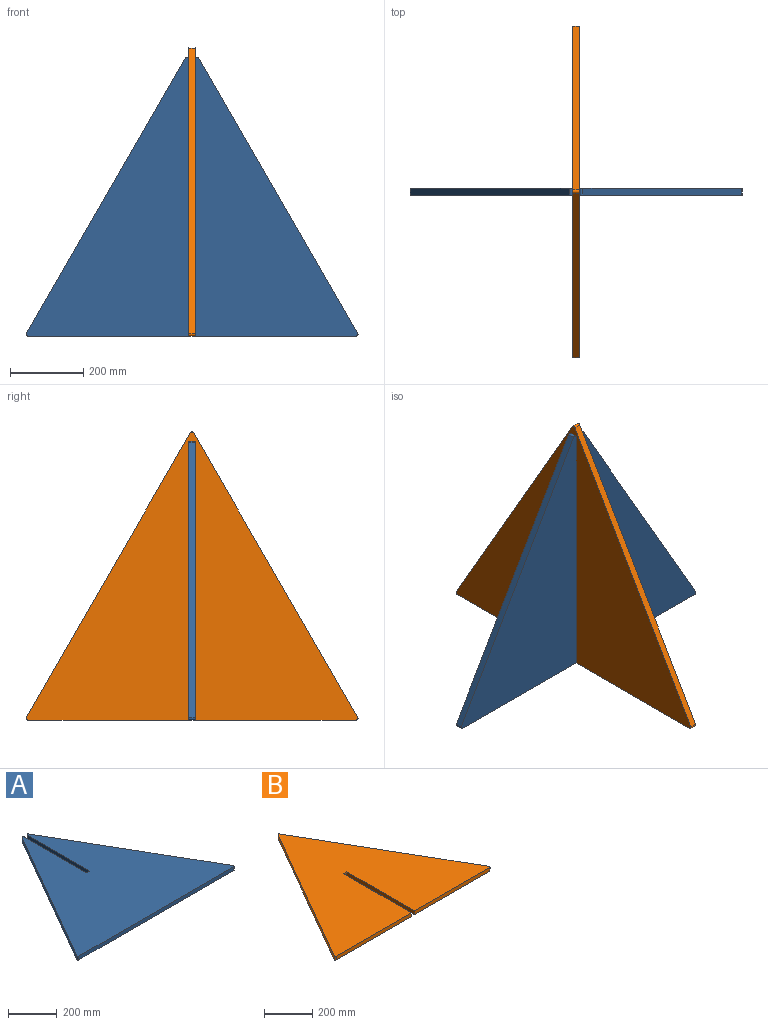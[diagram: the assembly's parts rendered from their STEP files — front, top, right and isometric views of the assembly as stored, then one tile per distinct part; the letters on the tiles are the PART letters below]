
ASSEMBLY  parts=2 mates=1
PART A: 12 faces, bbox 907x761.5x19.1 mm
  f0: plane 906.96x761.52mm, normal (0,0,1), area 354507.7mm2, adj f2,f3,f4,f5,f6,f7,f8,f9
  f1: plane 906.96x761.52mm, normal (0,0,-1), area 354507.7mm2, adj f2,f3,f4,f5,f6,f7,f8,f9
  f2: plane 751.36x433.8mm, normal (-0.87,0.5,0), area 16527.6mm2, adj f0,f1,f9,f10
  f3: plane 896.8x19.05mm, normal (0,-1,0), area 17084.1mm2, adj f0,f1,f10,f11
  f4: plane 751.36x433.8mm, normal (0.87,0.5,0), area 16527.6mm2, adj f0,f1,f8,f11
  f5: plane 360.49x19.05mm, normal (1,0,0), area 6867.3mm2, adj f0,f1,f6,f9
  f6: plane 19.05x19.05mm, normal (0,1,0), area 362.9mm2, adj f0,f1,f5,f7
  f7: plane 360.49x19.05mm, normal (-1,0,0), area 6867.3mm2, adj f0,f1,f6,f8
  f8: cylinder r=5.08mm len=19.05mm, axis (0,0,1), area 253.4mm2, adj f0,f1,f4,f7
  f9: cylinder r=5.08mm len=19.05mm, axis (0,0,1), area 253.4mm2, adj f0,f1,f2,f5
  f10: cylinder r=5.08mm len=19.05mm, axis (0,0,1), area 202.7mm2, adj f0,f1,f2,f3
  f11: cylinder r=5.08mm len=19.05mm, axis (0,0,-1), area 202.7mm2, adj f0,f1,f3,f4
PART B: 12 faces, bbox 907x786.8x19.1 mm
  f0: plane 438.88x19.05mm, normal (0,-1,0), area 8360.6mm2, adj f4,f5,f8,f11
  f1: plane 776.65x448.4mm, normal (-0.87,0.5,0), area 17084.1mm2, adj f4,f5,f9,f10
  f2: plane 438.88x19.05mm, normal (0,-1,0), area 8360.6mm2, adj f4,f5,f7,f10
  f3: plane 776.65x448.4mm, normal (0.87,0.5,0), area 17084.1mm2, adj f4,f5,f9,f11
  f4: plane 906.96x786.81mm, normal (0,0,1), area 354457.9mm2, adj f0,f1,f2,f3,f6,f7,f8,f9
  f5: plane 906.96x786.81mm, normal (0,0,-1), area 354457.9mm2, adj f0,f1,f2,f3,f6,f7,f8,f9
  f6: plane 19.05x19.05mm, normal (0,-1,0), area 362.9mm2, adj f4,f5,f7,f8
  f7: plane 395.95x19.05mm, normal (1,0,0), area 7542.8mm2, adj f2,f4,f5,f6
  f8: plane 395.95x19.05mm, normal (-1,0,0), area 7542.8mm2, adj f0,f4,f5,f6
  f9: cylinder r=5.08mm len=19.05mm, axis (0,0,1), area 202.7mm2, adj f1,f3,f4,f5
  f10: cylinder r=5.08mm len=19.05mm, axis (0,0,1), area 202.7mm2, adj f1,f2,f4,f5
  f11: cylinder r=5.08mm len=19.05mm, axis (0,0,-1), area 202.7mm2, adj f0,f3,f4,f5
PLACE A rot(axis=(1,0,0),90deg) t=(0,9.53,-393.41)mm
PLACE B rot(axis=(0.58,0.58,0.58),120deg) t=(-9.52,0,-393.41)mm
MATE fastened B.f6 <-> A.f6  axis (0,0,-1) through (0,0,2.54)mm
